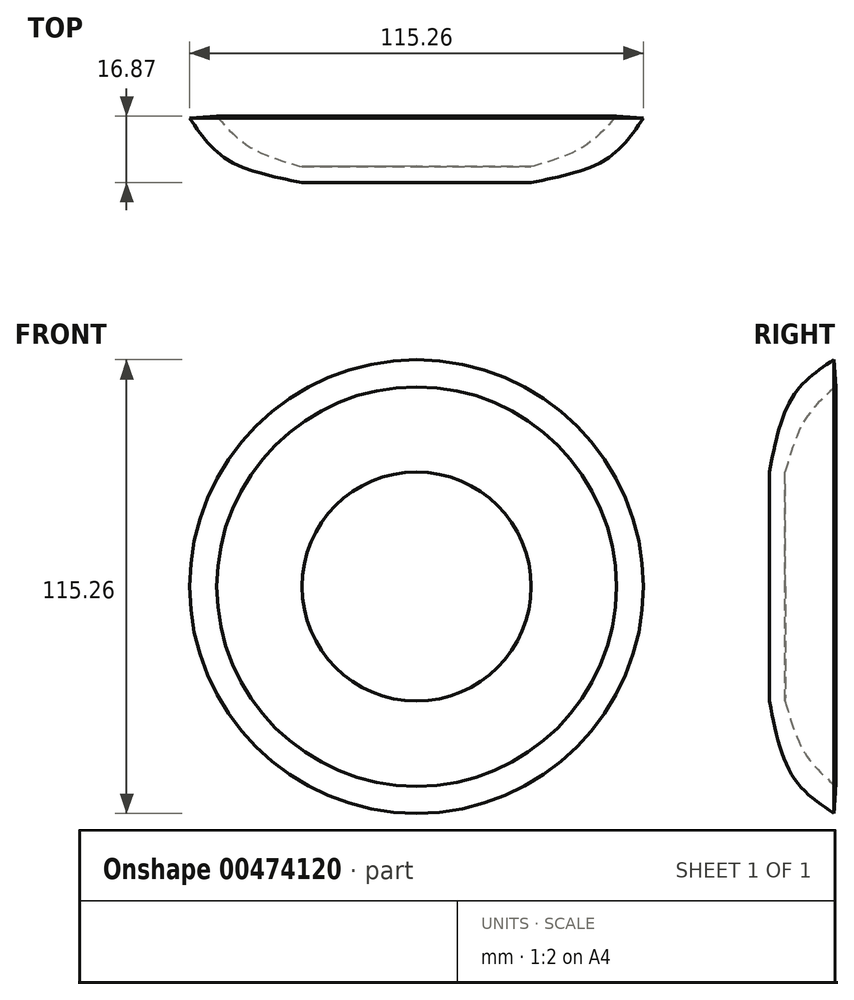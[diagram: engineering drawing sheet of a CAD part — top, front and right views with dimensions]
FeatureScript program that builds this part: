
annotation { "Feature Type Name" : "Feature", "Feature Type Description" : "" }
export const myFeature = defineFeature(function(context is Context, id is Id, definition is map)
    precondition{}
    {
        {
            var Q0;
            Q0=qCreatedBy(makeId("Top.planeOp"),FACE);
            var sketch = newSketch(context, id + "F0", { "sketchPlane" : qUnion([Q0])});
            skLineSegment(sketch, "E0", {"start": v(0, 0) * mm, "end": v(29.1, 0) * mm});
            skFitSpline(sketch, "E1", {"points": [v(29.1, 0) * mm, v(48.39, 6.05) * mm, v(57.63, 16.42) * mm], "startDerivative": vector(39.33, 7.83) * mm, "endDerivative": vector(17.02, 25.56) * mm});
            skFitSpline(sketch, "E2", {"points": [v(0, 4.13) * mm, v(29.1, 4.02) * mm], "startDerivative": vector(29.1, -0.11) * mm, "endDerivative": vector(29.1, -0.11) * mm});
            skFitSpline(sketch, "E3", {"points": [v(29.1, 4.02) * mm, v(42.41, 9.1) * mm, v(50.75, 16.87) * mm], "startDerivative": vector(27.2, 7.8) * mm, "endDerivative": vector(15.88, 18.09) * mm});
            skLineSegment(sketch, "E4", {"start": v(50.75, 16.87) * mm, "end": v(57.63, 16.42) * mm});
            skLineSegment(sketch, "E5", {"start": v(0, 4.13) * mm, "end": v(0, 0) * mm});
            skSolve(sketch);
        }
        {
            var Q0;
            Q0=sQuery(id+"F0.wireOp",EDGE,"E2");
            var Q1;
            Q1=sQuery(id+"F0.wireOp",EDGE,"E3");
            var Q2;
            Q2=sQuery(id+"F0.wireOp",EDGE,"E1");
            var Q3;
            Q3=sQuery(id+"F0.wireOp",EDGE,"E4");
            var Q4;
            Q4=sQuery(id+"F0.wireOp",EDGE,"E0");
            var Q5;
            Q5=sQuery(id+"F0.wireOp",EDGE,"E5");
            revolve(context, id + "F1", {"bodyType" : ToolBodyType.SURFACE, "surfaceEntities" : qUnion([Q0, Q1, Q2, Q3, Q4]), "axis" : qUnion([Q5]), "revolveType" : RevolveType.FULL});
        }
    });
